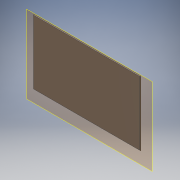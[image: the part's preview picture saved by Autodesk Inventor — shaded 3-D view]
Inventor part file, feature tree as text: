
AUTODESK INVENTOR PART (.ipt)
format: ipt  version: 2016 SP2 (Build 200236200, 236)  size: 102,912 bytes
history: native  units: mm
features: reference x12, plane x1, extrude x1, chamfer x1, sketch x1
ambient origin geometry x8: Origin, YZ Plane, XZ Plane, XY Plane, X Axis, Y Axis, Z Axis, Center Point
bodies: Body1 (feature_tree)
feature tree (16):
  plane  "Arbeitsebene1"
  extrude  "Extrusion2"  Depth=1.5mm
  chamfer  "Fase2"  Distance=0.1mm
  reference  "Referenz1"
  reference  "Referenz2"
  reference  "Referenz3"
  reference  "Referenz5"
  reference  "Referenz6"
  reference  "Referenz7"
  reference  "Referenz8"
  sketch  "Skizze2"  dims[d7=0.1mm d8=0.1mm d9=0.1mm d10=1.5mm d11=0.0mm d12=0.75mm d13=2.0mm d14=45.0deg]
  reference  "Referenz9"
  reference  "Referenz10"
  reference  "Referenz12"
  reference  "Referenz13"
  reference  "Referenz14"
